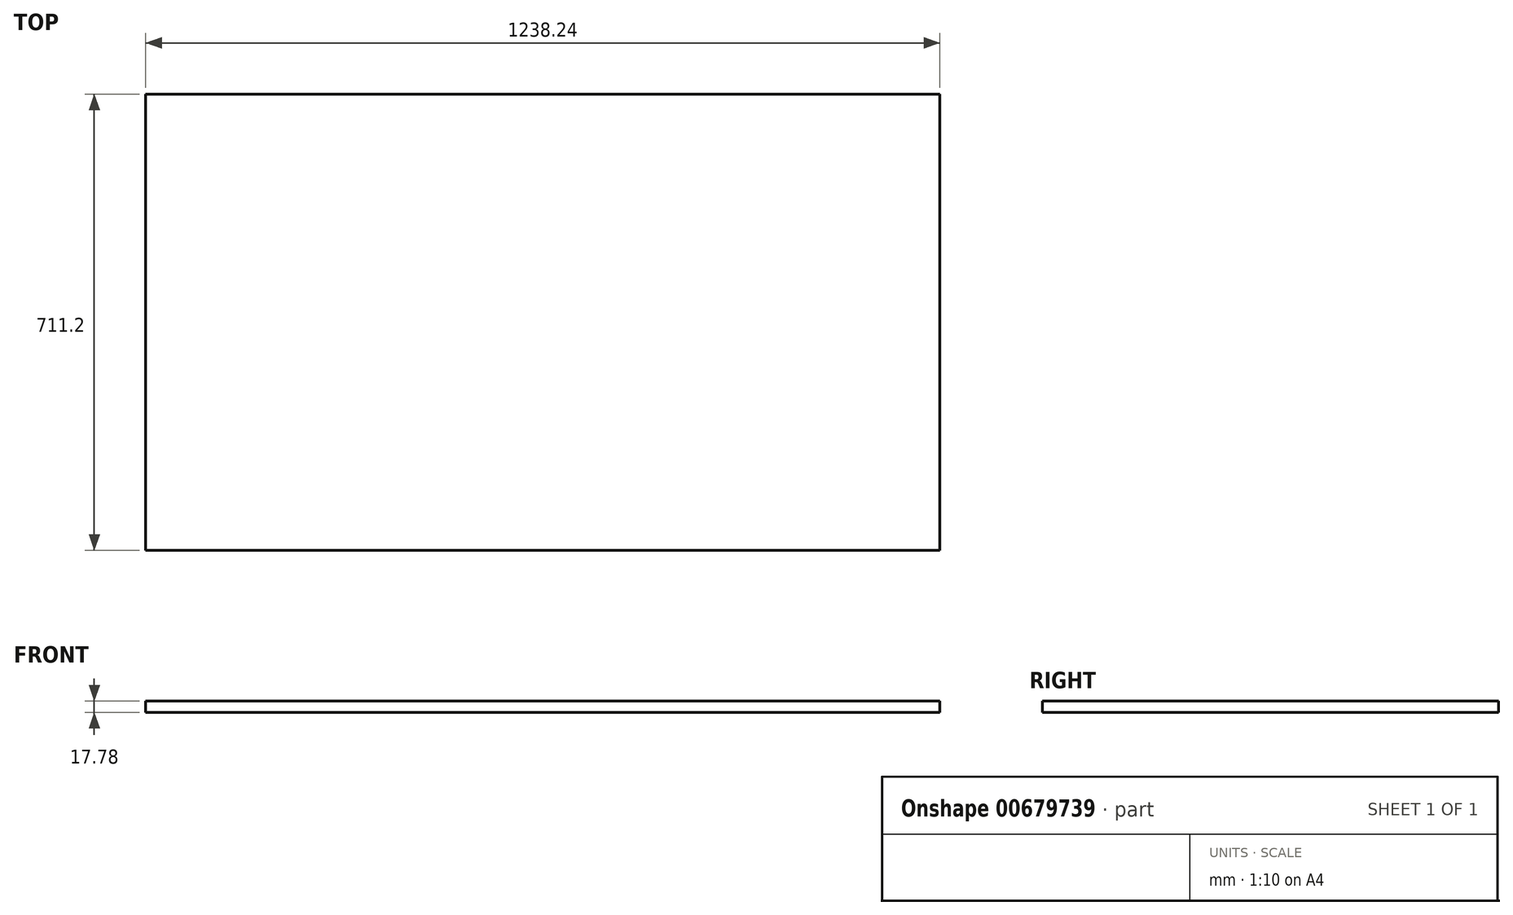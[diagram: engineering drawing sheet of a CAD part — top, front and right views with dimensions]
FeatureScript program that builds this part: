
annotation { "Feature Type Name" : "Feature", "Feature Type Description" : "" }
export const myFeature = defineFeature(function(context is Context, id is Id, definition is map)
    precondition{}
    {
        {
            var Q0;
            Q0=qCreatedBy(makeId("Top.planeOp"),FACE);
            var sketch = newSketch(context, id + "F0", { "sketchPlane" : qUnion([Q0])});
            skLineSegment(sketch, "E0.bottom", {"start": v(619.12, 355.6) * mm, "end": v(-619.12, 355.6) * mm});
            skLineSegment(sketch, "E0.top", {"start": v(619.12, -355.6) * mm, "end": v(-619.12, -355.6) * mm});
            skLineSegment(sketch, "E0.left", {"start": v(619.12, 355.6) * mm, "end": v(619.12, -355.6) * mm});
            skLineSegment(sketch, "E0.right", {"start": v(-619.12, 355.6) * mm, "end": v(-619.12, -355.6) * mm});
            skPoint(sketch, "E0.middle", {"position": v(0, 0) * mm});
            skSolve(sketch);
        }
        {
            var Q0;
            Q0=makeQuery(id+"F0.imprint","IMPRINT",FACE,{"disambiguationData":[TD([[makeQuery(id+"F0.imprint","IMPRINT",EDGE,{"derivedFrom":sQuery(id+"F0.wireOp",EDGE,"E0.bottom")}),1.0]])]});
            extrude(context, id + "F1", {"entities" : qUnion([Q0]), "endBound" : BoundingType.SYMMETRIC, "depth" : 17.78 * mm, "offsetDistance" : 25.4 * mm});
        }
    });
